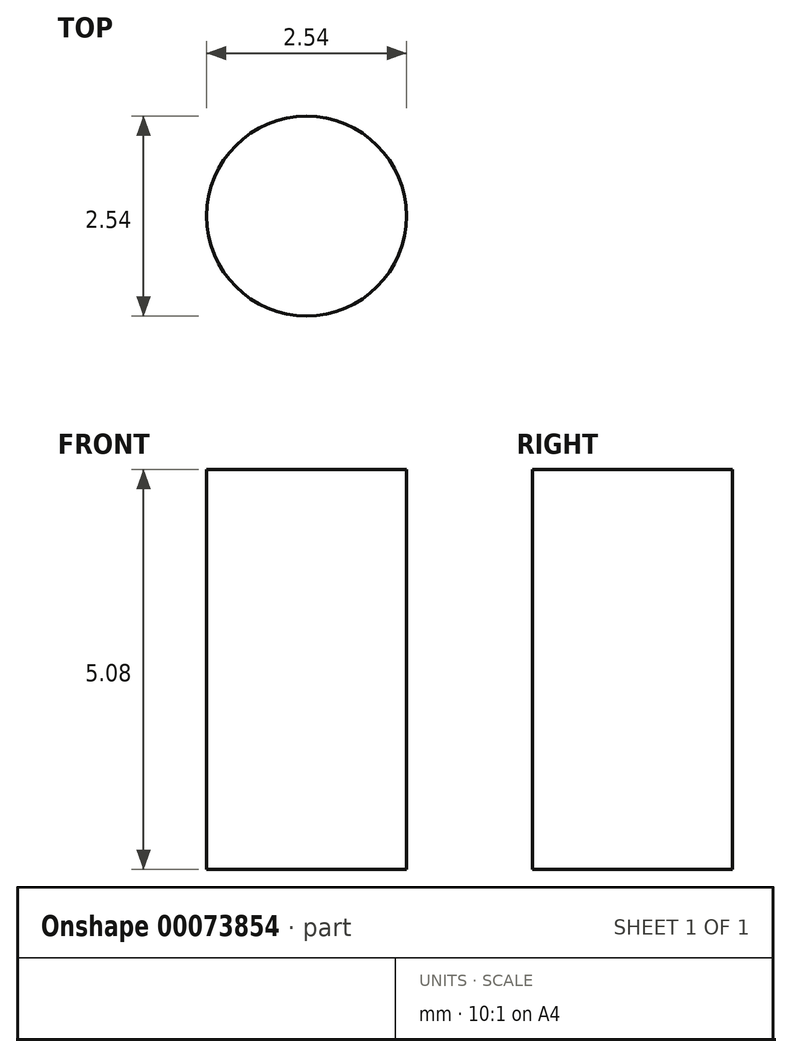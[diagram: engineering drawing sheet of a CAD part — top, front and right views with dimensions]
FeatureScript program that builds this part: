
annotation { "Feature Type Name" : "Feature", "Feature Type Description" : "" }
export const myFeature = defineFeature(function(context is Context, id is Id, definition is map)
    precondition{}
    {
        {
            var Q0;
            Q0=qCreatedBy(makeId("Front.planeOp"),FACE);
            var sketch = newSketch(context, id + "F0", { "sketchPlane" : qUnion([Q0])});
            skCircle(sketch, "E0", {"center": v(0, 0) * mm, "radius": 12.7 * mm});
            skSolve(sketch);
        }
        {
            var Q0;
            Q0=qCreatedBy(makeId("Top.planeOp"),FACE);
            var sketch = newSketch(context, id + "F1", { "sketchPlane" : qUnion([Q0])});
            skCircle(sketch, "E1", {"center": v(0, 0) * mm, "radius": 1.27 * mm});
            skSolve(sketch);
        }
        {
            var Q0;
            Q0 = qSketchRegion(id + "F1", true);
            extrude(context, id + "F2", {"entities" : qUnion([Q0]), "depth" : 2.54 * mm, "hasSecondDirection" : true, "secondDirectionOppositeDirection" : true, "secondDirectionDepth" : 2.54 * mm});
        }
    });
